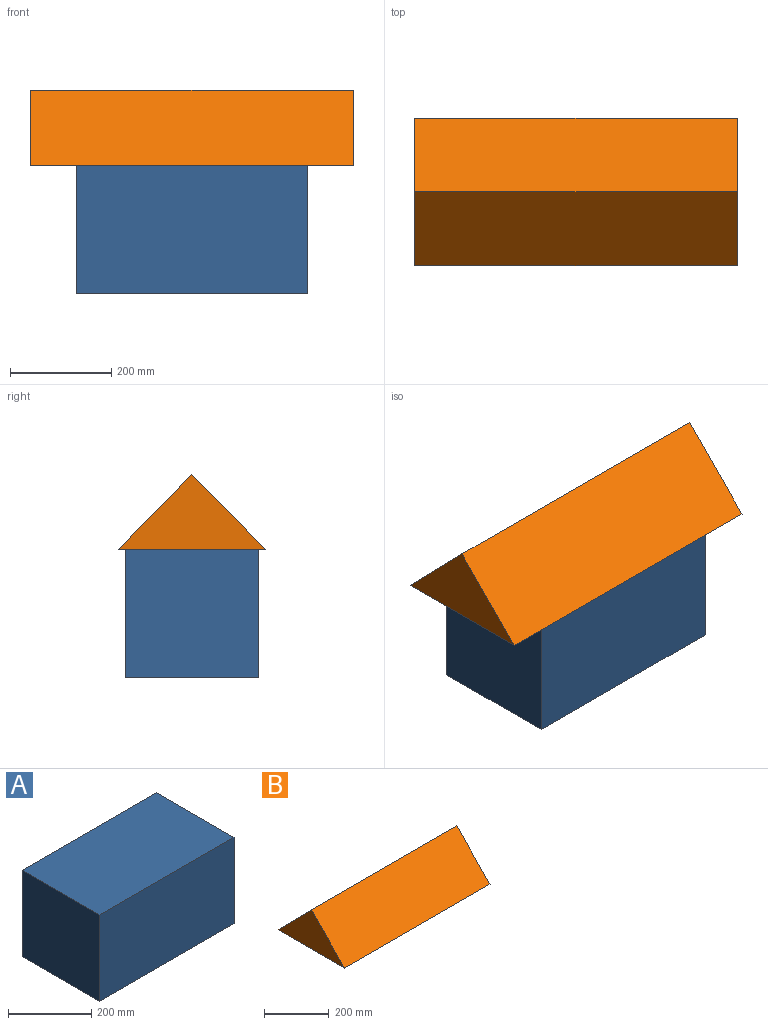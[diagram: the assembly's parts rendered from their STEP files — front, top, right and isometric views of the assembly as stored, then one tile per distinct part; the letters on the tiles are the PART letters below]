
ASSEMBLY  parts=2 mates=1
PART A: 6 faces, bbox 457.2x263.5x254 mm
  f0: plane 457.2x254mm, normal (0,-1,0), area 116128.8mm2, adj f1,f3,f4,f5
  f1: plane 263.53x254mm, normal (1,0,0), area 66935.4mm2, adj f0,f2,f4,f5
  f2: plane 457.2x254mm, normal (0,1,0), area 116128.8mm2, adj f1,f3,f4,f5
  f3: plane 263.53x254mm, normal (-1,0,0), area 66935.4mm2, adj f0,f2,f4,f5
  f4: plane 457.2x263.53mm, normal (0,0,1), area 120483.6mm2, adj f0,f1,f2,f3
  f5: plane 457.2x263.53mm, normal (0,0,-1), area 120483.6mm2, adj f0,f1,f2,f3
PART B: 5 faces, bbox 635x290.8x148.3 mm
  f0: plane 635x148.25mm, normal (0,-0.72,0.7), area 131639.3mm2, adj f1,f2,f3,f4
  f1: plane 635x290.84mm, normal (0,0,-1), area 184682mm2, adj f0,f2,f3,f4
  f2: plane 635x148.25mm, normal (0,0.71,0.7), area 132095.6mm2, adj f0,f1,f3,f4
  f3: plane 290.84x148.25mm, normal (1,0,0), area 21558.4mm2, adj f0,f1,f2
  f4: plane 290.84x148.25mm, normal (-1,0,0), area 21558.4mm2, adj f0,f1,f2
PLACE A at identity fixed
PLACE B rot(axis=(0,0,1),180deg) t=(0,0.51,-79.12)mm
MATE fastened B.f1 <-> A.f4  axis (0,0,-1) through (0,0,254)mm
